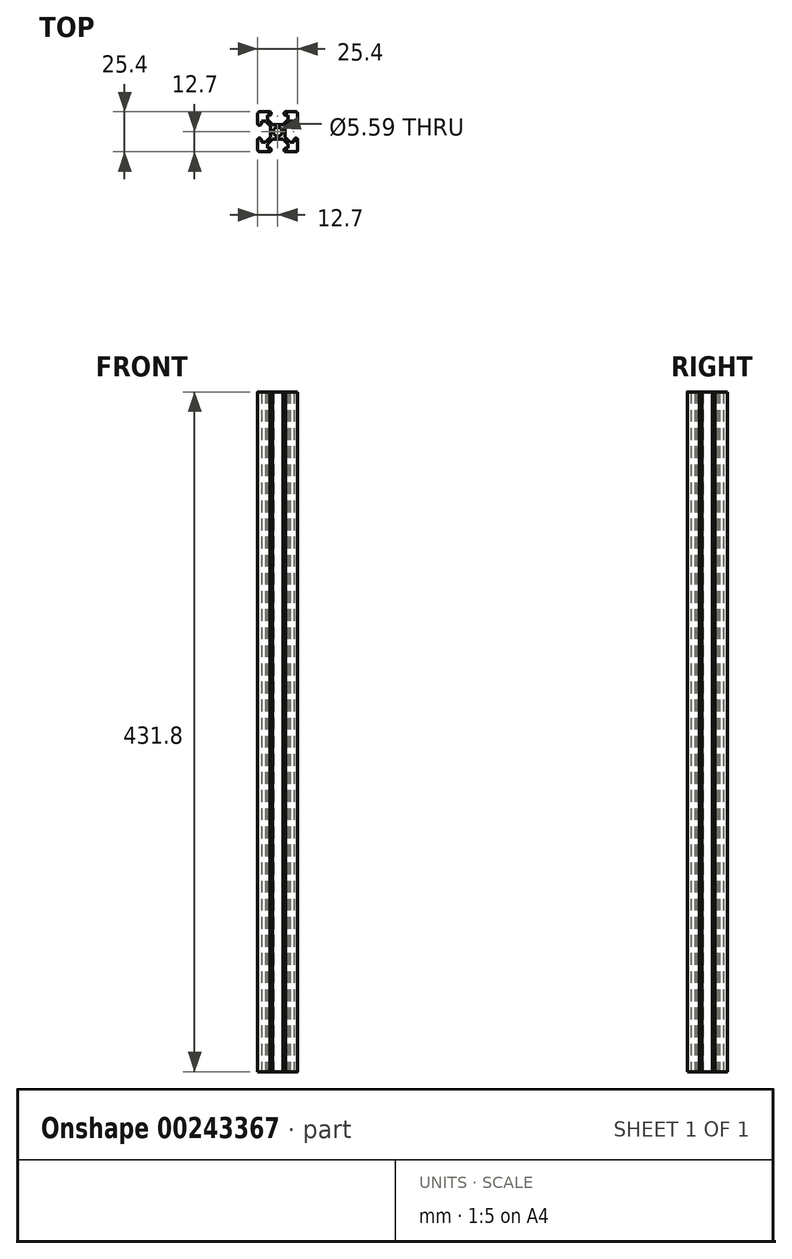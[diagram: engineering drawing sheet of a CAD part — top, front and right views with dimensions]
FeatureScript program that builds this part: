
annotation { "Feature Type Name" : "Feature", "Feature Type Description" : "" }
export const myFeature = defineFeature(function(context is Context, id is Id, definition is map)
    precondition{}
    {
        {
            var Q0;
            Q0=qCreatedBy(makeId("Top.planeOp"),FACE);
            var sketch = newSketch(context, id + "F0", { "sketchPlane" : qUnion([Q0])});
            skLineSegment(sketch, "E0.top", {"start": v(4.57, -4.57) * mm, "end": v(-4.57, -4.57) * mm});
            skLineSegment(sketch, "E0.left", {"start": v(4.57, 3.44) * mm, "end": v(4.57, -4.57) * mm});
            skLineSegment(sketch, "E0.right", {"start": v(-4.57, 4.57) * mm, "end": v(-4.57, -4.57) * mm});
            skPoint(sketch, "E0.middle", {"position": v(0, 0) * mm});
            skCircle(sketch, "E1", {"center": v(0, 0) * mm, "radius": 2.8 * mm});
            skLineSegment(sketch, "E2.bottom", {"start": v(11.43, 12.7) * mm, "end": v(4.92, 12.7) * mm});
            skLineSegment(sketch, "E2.left", {"start": v(12.7, 11.43) * mm, "end": v(12.7, 4.92) * mm});
            skPoint(sketch, "E2.middle", {"position": v(8.38, 8.38) * mm});
            skLineSegment(sketch, "E3", {"start": v(0, 0) * mm, "end": v(8.38, 8.38) * mm, "construction": true});
            skLineSegment(sketch, "E4", {"start": v(4.92, 10.41) * mm, "end": v(12.7, 10.41) * mm});
            skLineSegment(sketch, "E5", {"start": v(10.41, 12.7) * mm, "end": v(10.41, 4.92) * mm});
            skPoint(sketch, "E6.visualSharp", {"position": v(12.7, 12.7) * mm});
            skArc(sketch, "E6.filletArc", {"start": v(12.7, 11.43) * mm, "mid": v(12.33, 12.33) * mm, "end": v(11.43, 12.7) * mm});
            skLineSegment(sketch, "E7", {"start": v(5.59, 12.7) * mm, "end": v(5.59, 10.41) * mm, "construction": true});
            skLineSegment(sketch, "E8", {"start": v(10.41, 5.59) * mm, "end": v(12.7, 5.59) * mm, "construction": true});
            skArc(sketch, "E9", {"start": v(4.92, 12.7) * mm, "mid": v(4.06, 11.56) * mm, "end": v(4.92, 10.41) * mm});
            skLineSegment(sketch, "E10.bottom", {"start": v(10.41, 10.41) * mm, "end": v(6.6, 10.41) * mm});
            skLineSegment(sketch, "E10.top", {"start": v(10.41, 6.6) * mm, "end": v(7.74, 6.6) * mm});
            skLineSegment(sketch, "E10.left", {"start": v(10.41, 10.41) * mm, "end": v(10.41, 6.6) * mm});
            skLineSegment(sketch, "E10.right", {"start": v(6.6, 10.41) * mm, "end": v(6.6, 7.74) * mm});
            skArc(sketch, "E11", {"start": v(10.41, 4.92) * mm, "mid": v(11.56, 4.06) * mm, "end": v(12.7, 4.92) * mm});
            skLineSegment(sketch, "E12", {"start": v(6.6, 7.74) * mm, "end": v(3.44, 4.57) * mm});
            skLineSegment(sketch, "E13", {"start": v(7.74, 6.6) * mm, "end": v(4.57, 3.44) * mm});
            skLineSegment(sketch, "E14", {"start": v(3.36, 3.36) * mm, "end": v(3.93, 2.8) * mm, "construction": true});
            skLineSegment(sketch, "E15", {"start": v(3.19, 3.19) * mm, "end": v(2.62, 3.76) * mm, "construction": true});
            skLineSegment(sketch, "E16.trimOffspring", {"start": v(3.44, 4.57) * mm, "end": v(-4.57, 4.57) * mm});
            skPoint(sketch, "E0.bottom.start.orphan", {"position": v(4.57, 4.57) * mm});
            skPoint(sketch, "E17.orphan", {"position": v(4.06, 4.06) * mm});
            skPoint(sketch, "E18.orphan", {"position": v(4.06, 12.7) * mm});
            skPoint(sketch, "E19.orphan", {"position": v(12.7, 4.06) * mm});
            skLineSegment(sketch, "E20", {"start": v(0, 23.36) * mm, "end": v(0, -13.63) * mm, "construction": true});
            skLineSegment(sketch, "E21", {"start": v(-18.28, 0) * mm, "end": v(21.84, 0) * mm, "construction": true});
            skLineSegment(sketch, "E22.MirrorCS", {"start": v(-10.41, 5.59) * mm, "end": v(-12.7, 5.59) * mm, "construction": true});
            skLineSegment(sketch, "E23.MirrorCS", {"start": v(-10.41, 10.41) * mm, "end": v(-10.41, 6.6) * mm});
            skArc(sketch, "E24.MirrorCS", {"start": v(-12.7, 11.43) * mm, "mid": v(-12.33, 12.33) * mm, "end": v(-11.43, 12.7) * mm});
            skLineSegment(sketch, "E25.MirrorCS", {"start": v(-5.59, 12.7) * mm, "end": v(-5.59, 10.41) * mm, "construction": true});
            skLineSegment(sketch, "E26.MirrorCS", {"start": v(-3.36, 3.36) * mm, "end": v(-3.93, 2.8) * mm, "construction": true});
            skLineSegment(sketch, "E27.MirrorCS", {"start": v(-10.41, 10.41) * mm, "end": v(-6.6, 10.41) * mm});
            skLineSegment(sketch, "E28.MirrorCS", {"start": v(-3.19, 3.19) * mm, "end": v(-2.62, 3.76) * mm, "construction": true});
            skLineSegment(sketch, "E29.MirrorCS", {"start": v(0, 0) * mm, "end": v(-8.38, 8.38) * mm, "construction": true});
            skPoint(sketch, "E30.MirrorP", {"position": v(-4.06, 4.06) * mm});
            skLineSegment(sketch, "E31.MirrorCS", {"start": v(-4.57, 3.44) * mm, "end": v(-4.57, -4.57) * mm});
            skPoint(sketch, "E32.MirrorP", {"position": v(-4.57, 4.57) * mm});
            skLineSegment(sketch, "E33.MirrorCS", {"start": v(-10.41, 6.6) * mm, "end": v(-7.74, 6.6) * mm});
            skLineSegment(sketch, "E34.MirrorCS", {"start": v(-6.6, 7.74) * mm, "end": v(-3.44, 4.57) * mm});
            skLineSegment(sketch, "E35.MirrorCS", {"start": v(-11.43, 12.7) * mm, "end": v(-4.92, 12.7) * mm});
            skArc(sketch, "E36.MirrorCS", {"start": v(-4.92, 12.7) * mm, "mid": v(-4.06, 11.56) * mm, "end": v(-4.92, 10.41) * mm});
            skLineSegment(sketch, "E37.MirrorCS", {"start": v(-3.44, 4.57) * mm, "end": v(4.57, 4.57) * mm});
            skArc(sketch, "E38.MirrorCS", {"start": v(-10.41, 4.92) * mm, "mid": v(-11.56, 4.06) * mm, "end": v(-12.7, 4.92) * mm});
            skPoint(sketch, "E39.MirrorP", {"position": v(-4.06, 12.7) * mm});
            skLineSegment(sketch, "E40.MirrorCS", {"start": v(-4.57, -4.57) * mm, "end": v(4.57, -4.57) * mm});
            skLineSegment(sketch, "E41.MirrorCS", {"start": v(-12.7, 11.43) * mm, "end": v(-12.7, 4.92) * mm});
            skPoint(sketch, "E42.MirrorP", {"position": v(-12.7, 12.7) * mm});
            skPoint(sketch, "E43.MirrorP", {"position": v(-12.7, 4.06) * mm});
            skLineSegment(sketch, "E44.MirrorCS", {"start": v(-10.41, 12.7) * mm, "end": v(-10.41, 4.92) * mm});
            skLineSegment(sketch, "E45.MirrorCS", {"start": v(-7.74, 6.6) * mm, "end": v(-4.57, 3.44) * mm});
            skLineSegment(sketch, "E46.MirrorCS", {"start": v(-4.92, 10.41) * mm, "end": v(-12.7, 10.41) * mm});
            skLineSegment(sketch, "E47.MirrorCS", {"start": v(4.57, 4.57) * mm, "end": v(4.57, -4.57) * mm});
            skPoint(sketch, "E48.MirrorP", {"position": v(-8.38, 8.38) * mm});
            skLineSegment(sketch, "E49.MirrorCS", {"start": v(-6.6, 10.41) * mm, "end": v(-6.6, 7.74) * mm});
            skLineSegment(sketch, "E50.MirrorCS", {"start": v(3.36, -3.36) * mm, "end": v(3.93, -2.8) * mm, "construction": true});
            skLineSegment(sketch, "E51.MirrorCS", {"start": v(3.19, -3.19) * mm, "end": v(2.62, -3.76) * mm, "construction": true});
            skArc(sketch, "E52.MirrorCS", {"start": v(-12.7, -11.43) * mm, "mid": v(-12.33, -12.33) * mm, "end": v(-11.43, -12.7) * mm});
            skLineSegment(sketch, "E53.MirrorCS", {"start": v(-5.59, -12.7) * mm, "end": v(-5.59, -10.41) * mm, "construction": true});
            skLineSegment(sketch, "E54.MirrorCS", {"start": v(3.44, -4.57) * mm, "end": v(-4.57, -4.57) * mm});
            skLineSegment(sketch, "E55.MirrorCS", {"start": v(-10.41, -5.59) * mm, "end": v(-12.7, -5.59) * mm, "construction": true});
            skLineSegment(sketch, "E56.MirrorCS", {"start": v(4.57, 4.57) * mm, "end": v(-4.57, 4.57) * mm});
            skLineSegment(sketch, "E57.MirrorCS", {"start": v(-3.19, -3.19) * mm, "end": v(-2.62, -3.76) * mm, "construction": true});
            skLineSegment(sketch, "E58.MirrorCS", {"start": v(10.41, -10.41) * mm, "end": v(6.6, -10.41) * mm});
            skLineSegment(sketch, "E59.MirrorCS", {"start": v(10.41, -10.41) * mm, "end": v(10.41, -6.6) * mm});
            skLineSegment(sketch, "E60.MirrorCS", {"start": v(5.59, -12.7) * mm, "end": v(5.59, -10.41) * mm, "construction": true});
            skArc(sketch, "E61.MirrorCS", {"start": v(12.7, -11.43) * mm, "mid": v(12.33, -12.33) * mm, "end": v(11.43, -12.7) * mm});
            skLineSegment(sketch, "E62.MirrorCS", {"start": v(-3.36, -3.36) * mm, "end": v(-3.93, -2.8) * mm, "construction": true});
            skLineSegment(sketch, "E63.MirrorCS", {"start": v(10.41, -5.59) * mm, "end": v(12.7, -5.59) * mm, "construction": true});
            skLineSegment(sketch, "E64.MirrorCS", {"start": v(-4.57, -4.57) * mm, "end": v(-4.57, 4.57) * mm});
            skLineSegment(sketch, "E65.MirrorCS", {"start": v(4.57, -3.44) * mm, "end": v(4.57, 4.57) * mm});
            skLineSegment(sketch, "E66.MirrorCS", {"start": v(-10.41, -10.41) * mm, "end": v(-10.41, -6.6) * mm});
            skLineSegment(sketch, "E67.MirrorCS", {"start": v(12.7, -11.43) * mm, "end": v(12.7, -4.92) * mm});
            skPoint(sketch, "E68.MirrorP", {"position": v(12.7, -4.06) * mm});
            skPoint(sketch, "E69.MirrorP", {"position": v(12.7, -12.7) * mm});
            skLineSegment(sketch, "E70.MirrorCS", {"start": v(-4.57, 4.57) * mm, "end": v(4.57, 4.57) * mm});
            skLineSegment(sketch, "E71.MirrorCS", {"start": v(-7.74, -6.6) * mm, "end": v(-4.57, -3.44) * mm});
            skLineSegment(sketch, "E72.MirrorCS", {"start": v(-12.7, -11.43) * mm, "end": v(-12.7, -4.92) * mm});
            skLineSegment(sketch, "E73.MirrorCS", {"start": v(-6.6, -10.41) * mm, "end": v(-6.6, -7.74) * mm});
            skLineSegment(sketch, "E74.MirrorCS", {"start": v(6.6, -7.74) * mm, "end": v(3.44, -4.57) * mm});
            skLineSegment(sketch, "E75.MirrorCS", {"start": v(-3.44, -4.57) * mm, "end": v(4.57, -4.57) * mm});
            skPoint(sketch, "E76.MirrorP", {"position": v(-4.57, -4.57) * mm});
            skLineSegment(sketch, "E77.MirrorCS", {"start": v(-10.41, -12.7) * mm, "end": v(-10.41, -4.92) * mm});
            skPoint(sketch, "E78.MirrorP", {"position": v(-8.38, -8.38) * mm});
            skLineSegment(sketch, "E79.MirrorCS", {"start": v(-10.41, -6.6) * mm, "end": v(-7.74, -6.6) * mm});
            skLineSegment(sketch, "E80.MirrorCS", {"start": v(4.92, -10.41) * mm, "end": v(12.7, -10.41) * mm});
            skPoint(sketch, "E81.MirrorP", {"position": v(4.06, -4.06) * mm});
            skLineSegment(sketch, "E82.MirrorCS", {"start": v(-10.41, -10.41) * mm, "end": v(-6.6, -10.41) * mm});
            skArc(sketch, "E83.MirrorCS", {"start": v(-4.92, -12.7) * mm, "mid": v(-4.06, -11.56) * mm, "end": v(-4.92, -10.41) * mm});
            skLineSegment(sketch, "E84.MirrorCS", {"start": v(-11.43, -12.7) * mm, "end": v(-4.92, -12.7) * mm});
            skPoint(sketch, "E85.MirrorP", {"position": v(4.57, -4.57) * mm});
            skLineSegment(sketch, "E86.MirrorCS", {"start": v(4.57, -4.57) * mm, "end": v(4.57, 4.57) * mm});
            skLineSegment(sketch, "E87.MirrorCS", {"start": v(-6.6, -7.74) * mm, "end": v(-3.44, -4.57) * mm});
            skLineSegment(sketch, "E88.MirrorCS", {"start": v(0, 0) * mm, "end": v(8.38, -8.38) * mm, "construction": true});
            skArc(sketch, "E89.MirrorCS", {"start": v(-10.41, -4.92) * mm, "mid": v(-11.56, -4.06) * mm, "end": v(-12.7, -4.92) * mm});
            skLineSegment(sketch, "E90.MirrorCS", {"start": v(-4.92, -10.41) * mm, "end": v(-12.7, -10.41) * mm});
            skArc(sketch, "E91.MirrorCS", {"start": v(10.41, -4.92) * mm, "mid": v(11.56, -4.06) * mm, "end": v(12.7, -4.92) * mm});
            skPoint(sketch, "E92.MirrorP", {"position": v(-12.7, -4.06) * mm});
            skLineSegment(sketch, "E93.MirrorCS", {"start": v(10.41, -12.7) * mm, "end": v(10.41, -4.92) * mm});
            skLineSegment(sketch, "E94.MirrorCS", {"start": v(0, 0) * mm, "end": v(-8.38, -8.38) * mm, "construction": true});
            skLineSegment(sketch, "E95.MirrorCS", {"start": v(-4.57, -3.44) * mm, "end": v(-4.57, 4.57) * mm});
            skPoint(sketch, "E96.MirrorP", {"position": v(-4.06, -4.06) * mm});
            skPoint(sketch, "E97.MirrorP", {"position": v(-4.06, -12.7) * mm});
            skLineSegment(sketch, "E98.MirrorCS", {"start": v(10.41, -6.6) * mm, "end": v(7.74, -6.6) * mm});
            skArc(sketch, "E99.MirrorCS", {"start": v(4.92, -12.7) * mm, "mid": v(4.06, -11.56) * mm, "end": v(4.92, -10.41) * mm});
            skLineSegment(sketch, "E100.MirrorCS", {"start": v(11.43, -12.7) * mm, "end": v(4.92, -12.7) * mm});
            skLineSegment(sketch, "E101.MirrorCS", {"start": v(7.74, -6.6) * mm, "end": v(4.57, -3.44) * mm});
            skPoint(sketch, "E102.MirrorP", {"position": v(-12.7, -12.7) * mm});
            skPoint(sketch, "E103.MirrorP", {"position": v(4.06, -12.7) * mm});
            skPoint(sketch, "E104.MirrorP", {"position": v(8.38, -8.38) * mm});
            skLineSegment(sketch, "E105.MirrorCS", {"start": v(6.6, -10.41) * mm, "end": v(6.6, -7.74) * mm});
            skSolve(sketch);
        }
        {
            var Q0;
            Q0 = qSketchRegion(id + "F0", true);
            extrude(context, id + "F1", {"entities" : qUnion([Q0]), "depth" : 431.8 * mm});
        }
    });
